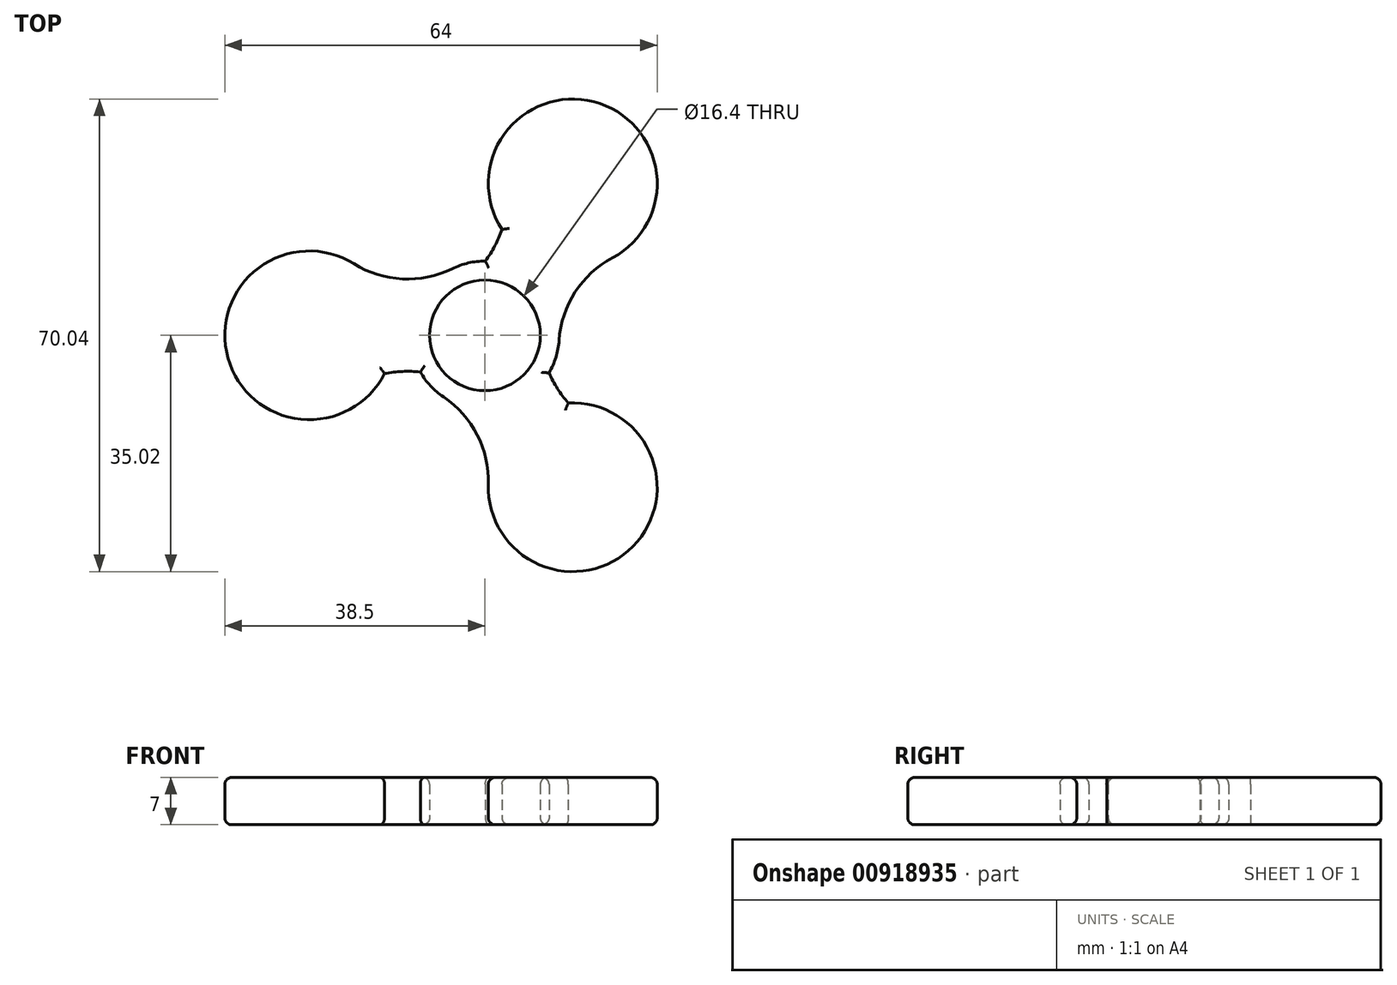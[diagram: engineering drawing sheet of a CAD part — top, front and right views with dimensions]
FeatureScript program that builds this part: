
annotation { "Feature Type Name" : "Feature", "Feature Type Description" : "" }
export const myFeature = defineFeature(function(context is Context, id is Id, definition is map)
    precondition{}
    {
        {
            var Q0;
            Q0=qCreatedBy(makeId("Top.planeOp"),FACE);
            var sketch = newSketch(context, id + "F0", { "sketchPlane" : qUnion([Q0])});
            skCircle(sketch, "E0", {"center": v(0, 0) * mm, "radius": 8.2 * mm});
            skCircle(sketch, "E1", {"center": v(0, 0) * mm, "radius": 11 * mm});
            skLineSegment(sketch, "E2", {"start": v(0, 0) * mm, "end": v(-26, 0) * mm, "construction": true});
            skCircle(sketch, "E3", {"center": v(-26, 0) * mm, "radius": 12.5 * mm});
            skArc(sketch, "E4", {"start": v(-19.39, 10.6) * mm, "mid": v(-12.21, 8.36) * mm, "end": v(-4.85, 9.87) * mm});
            skArc(sketch, "E5", {"start": v(-14.86, 5.66) * mm, "mid": v(-12.22, 5.36) * mm, "end": v(-9.56, 5.44) * mm});
            skArc(sketch, "E6.MirrorCS", {"start": v(-14.86, -5.66) * mm, "mid": v(-12.22, -5.36) * mm, "end": v(-9.56, -5.44) * mm});
            skArc(sketch, "E7.MirrorCS", {"start": v(-19.39, -10.6) * mm, "mid": v(-12.21, -8.36) * mm, "end": v(-4.85, -9.87) * mm});
            skLineSegment(sketch, "E8.1.0", {"start": v(0, 0) * mm, "end": v(13, -22.52) * mm, "construction": true});
            skCircle(sketch, "E8.1.1", {"center": v(13, -22.52) * mm, "radius": 12.5 * mm});
            skArc(sketch, "E8.1.2", {"start": v(0.5, -22.1) * mm, "mid": v(-1.13, -14.76) * mm, "end": v(-6.13, -9.13) * mm});
            skArc(sketch, "E8.1.3", {"start": v(2.52, -15.7) * mm, "mid": v(1.47, -13.26) * mm, "end": v(0.07, -11) * mm});
            skArc(sketch, "E8.1.4", {"start": v(12.33, -10.03) * mm, "mid": v(10.75, -7.9) * mm, "end": v(9.5, -5.56) * mm});
            skArc(sketch, "E8.1.5", {"start": v(18.88, -11.49) * mm, "mid": v(13.35, -6.4) * mm, "end": v(10.98, 0.74) * mm});
            skLineSegment(sketch, "E8.2.0", {"start": v(0, 0) * mm, "end": v(13, 22.52) * mm, "construction": true});
            skCircle(sketch, "E8.2.1", {"center": v(13, 22.52) * mm, "radius": 12.5 * mm});
            skArc(sketch, "E8.2.2", {"start": v(18.88, 11.49) * mm, "mid": v(13.35, 6.4) * mm, "end": v(10.98, -0.74) * mm});
            skArc(sketch, "E8.2.3", {"start": v(12.33, 10.03) * mm, "mid": v(10.75, 7.9) * mm, "end": v(9.5, 5.56) * mm});
            skArc(sketch, "E8.2.4", {"start": v(2.52, 15.7) * mm, "mid": v(1.47, 13.26) * mm, "end": v(0.07, 11) * mm});
            skArc(sketch, "E8.2.5", {"start": v(0.5, 22.1) * mm, "mid": v(-1.13, 14.76) * mm, "end": v(-6.13, 9.13) * mm});
            skSolve(sketch);
        }
        {
            var Q0;
            {var subQ0=sQuery(id+"F0.wireOp",EDGE,"E3");var subQ4=sQuery(id+"F0.wireOp",EDGE,"E1");var subQ5=makeQuery(id+"F0.imprint","INTERSECT",VERTEX,{"disambiguationData":[OD(0.0)],"derivedFrom":[subQ4,subQ0]});Q0=makeQuery(id+"F0.imprint","IMPRINT",FACE,{"disambiguationData":[TD([[makeQuery(id+"F0.imprint","IMPRINT",EDGE,{"disambiguationData":[TD([[subQ5,-1.0]])],"derivedFrom":subQ4}),-1.0]])]});}
            var Q1;
            {var subQ0=sQuery(id+"F0.wireOp",EDGE,"E3");var subQ1=sQuery(id+"F0.wireOp",EDGE,"E1");var subQ2=makeQuery(id+"F0.imprint","INTERSECT",VERTEX,{"disambiguationData":[OD(0.0)],"derivedFrom":[subQ1,subQ0]});Q1=makeQuery(id+"F0.imprint","IMPRINT",FACE,{"disambiguationData":[TD([[makeQuery(id+"F0.imprint","IMPRINT",EDGE,{"disambiguationData":[TD([[subQ2,-1.0]])],"derivedFrom":subQ1}),1.0]])]});}
            var Q2;
            Q2=makeQuery(id+"F0.imprint","IMPRINT",FACE,{"disambiguationData":[TD([[makeQuery(id+"F0.imprint","IMPRINT",EDGE,{"derivedFrom":sQuery(id+"F0.wireOp",EDGE,"E0")}),-1.0]])]});
            var Q3;
            {var subQ0=sQuery(id+"F0.wireOp",EDGE,"E4");Q3=makeQuery(id+"F0.imprint","IMPRINT",FACE,{"disambiguationData":[TD([[makeQuery(id+"F0.imprint","IMPRINT",EDGE,{"derivedFrom":subQ0}),-1.0]])]});}
            var Q4;
            {var subQ0=sQuery(id+"F0.wireOp",EDGE,"E8.2.4");Q4=makeQuery(id+"F0.imprint","IMPRINT",FACE,{"disambiguationData":[TD([[makeQuery(id+"F0.imprint","IMPRINT",EDGE,{"derivedFrom":subQ0}),-1.0]])]});}
            var Q5;
            {var subQ0=sQuery(id+"F0.wireOp",EDGE,"E8.2.1");var subQ4=sQuery(id+"F0.wireOp",EDGE,"E1");var subQ5=makeQuery(id+"F0.imprint","INTERSECT",VERTEX,{"disambiguationData":[OD(0.0)],"derivedFrom":[subQ4,subQ0]});Q5=makeQuery(id+"F0.imprint","IMPRINT",FACE,{"disambiguationData":[TD([[makeQuery(id+"F0.imprint","IMPRINT",EDGE,{"disambiguationData":[TD([[subQ5,-1.0]])],"derivedFrom":subQ4}),-1.0]])]});}
            var Q6;
            {var subQ0=sQuery(id+"F0.wireOp",EDGE,"E8.2.1");var subQ1=sQuery(id+"F0.wireOp",EDGE,"E1");var subQ2=makeQuery(id+"F0.imprint","INTERSECT",VERTEX,{"disambiguationData":[OD(0.0)],"derivedFrom":[subQ1,subQ0]});Q6=makeQuery(id+"F0.imprint","IMPRINT",FACE,{"disambiguationData":[TD([[makeQuery(id+"F0.imprint","IMPRINT",EDGE,{"disambiguationData":[TD([[subQ2,-1.0]])],"derivedFrom":subQ1}),1.0]])]});}
            var Q7;
            {var subQ0=sQuery(id+"F0.wireOp",EDGE,"E8.2.2");Q7=makeQuery(id+"F0.imprint","IMPRINT",FACE,{"disambiguationData":[TD([[makeQuery(id+"F0.imprint","IMPRINT",EDGE,{"derivedFrom":subQ0}),-1.0]])]});}
            var Q8;
            {var subQ0=sQuery(id+"F0.wireOp",EDGE,"E8.1.4");Q8=makeQuery(id+"F0.imprint","IMPRINT",FACE,{"disambiguationData":[TD([[makeQuery(id+"F0.imprint","IMPRINT",EDGE,{"derivedFrom":subQ0}),-1.0]])]});}
            var Q9;
            {var subQ0=sQuery(id+"F0.wireOp",EDGE,"E8.1.1");var subQ4=sQuery(id+"F0.wireOp",EDGE,"E1");var subQ5=makeQuery(id+"F0.imprint","INTERSECT",VERTEX,{"disambiguationData":[OD(0.0)],"derivedFrom":[subQ4,subQ0]});Q9=makeQuery(id+"F0.imprint","IMPRINT",FACE,{"disambiguationData":[TD([[makeQuery(id+"F0.imprint","IMPRINT",EDGE,{"disambiguationData":[TD([[subQ5,-1.0]])],"derivedFrom":subQ4}),-1.0]])]});}
            var Q10;
            {var subQ0=sQuery(id+"F0.wireOp",EDGE,"E8.1.1");var subQ1=sQuery(id+"F0.wireOp",EDGE,"E1");var subQ2=makeQuery(id+"F0.imprint","INTERSECT",VERTEX,{"disambiguationData":[OD(0.0)],"derivedFrom":[subQ1,subQ0]});Q10=makeQuery(id+"F0.imprint","IMPRINT",FACE,{"disambiguationData":[TD([[makeQuery(id+"F0.imprint","IMPRINT",EDGE,{"disambiguationData":[TD([[subQ2,-1.0]])],"derivedFrom":subQ1}),1.0]])]});}
            var Q11;
            {var subQ0=sQuery(id+"F0.wireOp",EDGE,"E8.1.2");Q11=makeQuery(id+"F0.imprint","IMPRINT",FACE,{"disambiguationData":[TD([[makeQuery(id+"F0.imprint","IMPRINT",EDGE,{"derivedFrom":subQ0}),-1.0]])]});}
            var Q12;
            {var subQ0=sQuery(id+"F0.wireOp",EDGE,"E6.MirrorCS");Q12=makeQuery(id+"F0.imprint","IMPRINT",FACE,{"disambiguationData":[TD([[makeQuery(id+"F0.imprint","IMPRINT",EDGE,{"derivedFrom":subQ0}),-1.0]])]});}
            var Q13;
            {var subQ0=sQuery(id+"F0.wireOp",EDGE,"E5");Q13=makeQuery(id+"F0.imprint","IMPRINT",FACE,{"disambiguationData":[TD([[makeQuery(id+"F0.imprint","IMPRINT",EDGE,{"derivedFrom":subQ0}),1.0]])]});}
            var Q14;
            {var subQ0=sQuery(id+"F0.wireOp",EDGE,"E3");var subQ1=makeQuery(id+"F0.imprint","INTERSECT",VERTEX,{"derivedFrom":[subQ0,sQuery(id+"F0.wireOp",EDGE,"E4")]});Q14=makeQuery(id+"F0.imprint","IMPRINT",FACE,{"disambiguationData":[TD([[makeQuery(id+"F0.imprint","IMPRINT",EDGE,{"disambiguationData":[TD([[subQ1,1.0]])],"derivedFrom":subQ0}),1.0]])]});}
            var Q15;
            {var subQ0=sQuery(id+"F0.wireOp",EDGE,"E8.2.1");var subQ1=makeQuery(id+"F0.imprint","INTERSECT",VERTEX,{"derivedFrom":[subQ0,sQuery(id+"F0.wireOp",EDGE,"E8.2.2")]});Q15=makeQuery(id+"F0.imprint","IMPRINT",FACE,{"disambiguationData":[TD([[makeQuery(id+"F0.imprint","IMPRINT",EDGE,{"disambiguationData":[TD([[subQ1,1.0]])],"derivedFrom":subQ0}),1.0]])]});}
            var Q16;
            {var subQ3=sQuery(id+"F0.wireOp",EDGE,"E8.2.3");Q16=makeQuery(id+"F0.imprint","IMPRINT",FACE,{"disambiguationData":[TD([[makeQuery(id+"F0.imprint","IMPRINT",EDGE,{"derivedFrom":subQ3}),1.0]])]});}
            var Q17;
            {var subQ0=sQuery(id+"F0.wireOp",EDGE,"E8.1.1");var subQ1=makeQuery(id+"F0.imprint","INTERSECT",VERTEX,{"derivedFrom":[subQ0,sQuery(id+"F0.wireOp",EDGE,"E8.1.2")]});Q17=makeQuery(id+"F0.imprint","IMPRINT",FACE,{"disambiguationData":[TD([[makeQuery(id+"F0.imprint","IMPRINT",EDGE,{"disambiguationData":[TD([[subQ1,1.0]])],"derivedFrom":subQ0}),1.0]])]});}
            var Q18;
            {var subQ3=sQuery(id+"F0.wireOp",EDGE,"E8.1.3");Q18=makeQuery(id+"F0.imprint","IMPRINT",FACE,{"disambiguationData":[TD([[makeQuery(id+"F0.imprint","IMPRINT",EDGE,{"derivedFrom":subQ3}),1.0]])]});}
            extrude(context, id + "F1", {"entities" : qUnion([Q0, Q1, Q2, Q3, Q4, Q5, Q6, Q7, Q8, Q9, Q10, Q11, Q12, Q13, Q14, Q15, Q16, Q17, Q18]), "depth" : 7 * mm, "offsetDistance" : 25 * mm});
        }
        {
            var Q0;
            Q0=makeQuery(id+"F1.opExtrude","CAP_FACE",FACE,{"disambiguationData":[OSD([sQuery(id+"F0.wireOp",EDGE,"E0"),sQuery(id+"F0.wireOp",EDGE,"E1"),sQuery(id+"F0.wireOp",EDGE,"E3"),sQuery(id+"F0.wireOp",EDGE,"E4"),sQuery(id+"F0.wireOp",EDGE,"E5"),sQuery(id+"F0.wireOp",EDGE,"E6.MirrorCS"),sQuery(id+"F0.wireOp",EDGE,"E7.MirrorCS"),sQuery(id+"F0.wireOp",EDGE,"E8.1.1"),sQuery(id+"F0.wireOp",EDGE,"E8.1.2"),sQuery(id+"F0.wireOp",EDGE,"E8.1.3"),sQuery(id+"F0.wireOp",EDGE,"E8.1.4"),sQuery(id+"F0.wireOp",EDGE,"E8.1.5"),sQuery(id+"F0.wireOp",EDGE,"E8.2.1"),sQuery(id+"F0.wireOp",EDGE,"E8.2.2"),sQuery(id+"F0.wireOp",EDGE,"E8.2.3"),sQuery(id+"F0.wireOp",EDGE,"E8.2.4"),sQuery(id+"F0.wireOp",EDGE,"E8.2.5")])],"isStart":false});
            var Q1;
            Q1=makeQuery(id+"F1.opExtrude","CAP_FACE",FACE,{"disambiguationData":[OSD([sQuery(id+"F0.wireOp",EDGE,"E0"),sQuery(id+"F0.wireOp",EDGE,"E1"),sQuery(id+"F0.wireOp",EDGE,"E3"),sQuery(id+"F0.wireOp",EDGE,"E4"),sQuery(id+"F0.wireOp",EDGE,"E5"),sQuery(id+"F0.wireOp",EDGE,"E6.MirrorCS"),sQuery(id+"F0.wireOp",EDGE,"E7.MirrorCS"),sQuery(id+"F0.wireOp",EDGE,"E8.1.1"),sQuery(id+"F0.wireOp",EDGE,"E8.1.2"),sQuery(id+"F0.wireOp",EDGE,"E8.1.3"),sQuery(id+"F0.wireOp",EDGE,"E8.1.4"),sQuery(id+"F0.wireOp",EDGE,"E8.1.5"),sQuery(id+"F0.wireOp",EDGE,"E8.2.1"),sQuery(id+"F0.wireOp",EDGE,"E8.2.2"),sQuery(id+"F0.wireOp",EDGE,"E8.2.3"),sQuery(id+"F0.wireOp",EDGE,"E8.2.4"),sQuery(id+"F0.wireOp",EDGE,"E8.2.5")])],"isStart":true});
            fillet(context, id + "F2", {"entities" : qUnion([Q0, Q1]), "radius" : 1 * mm, "tangentPropagation" : true, "allowEdgeOverflow" : false});
        }
    });
